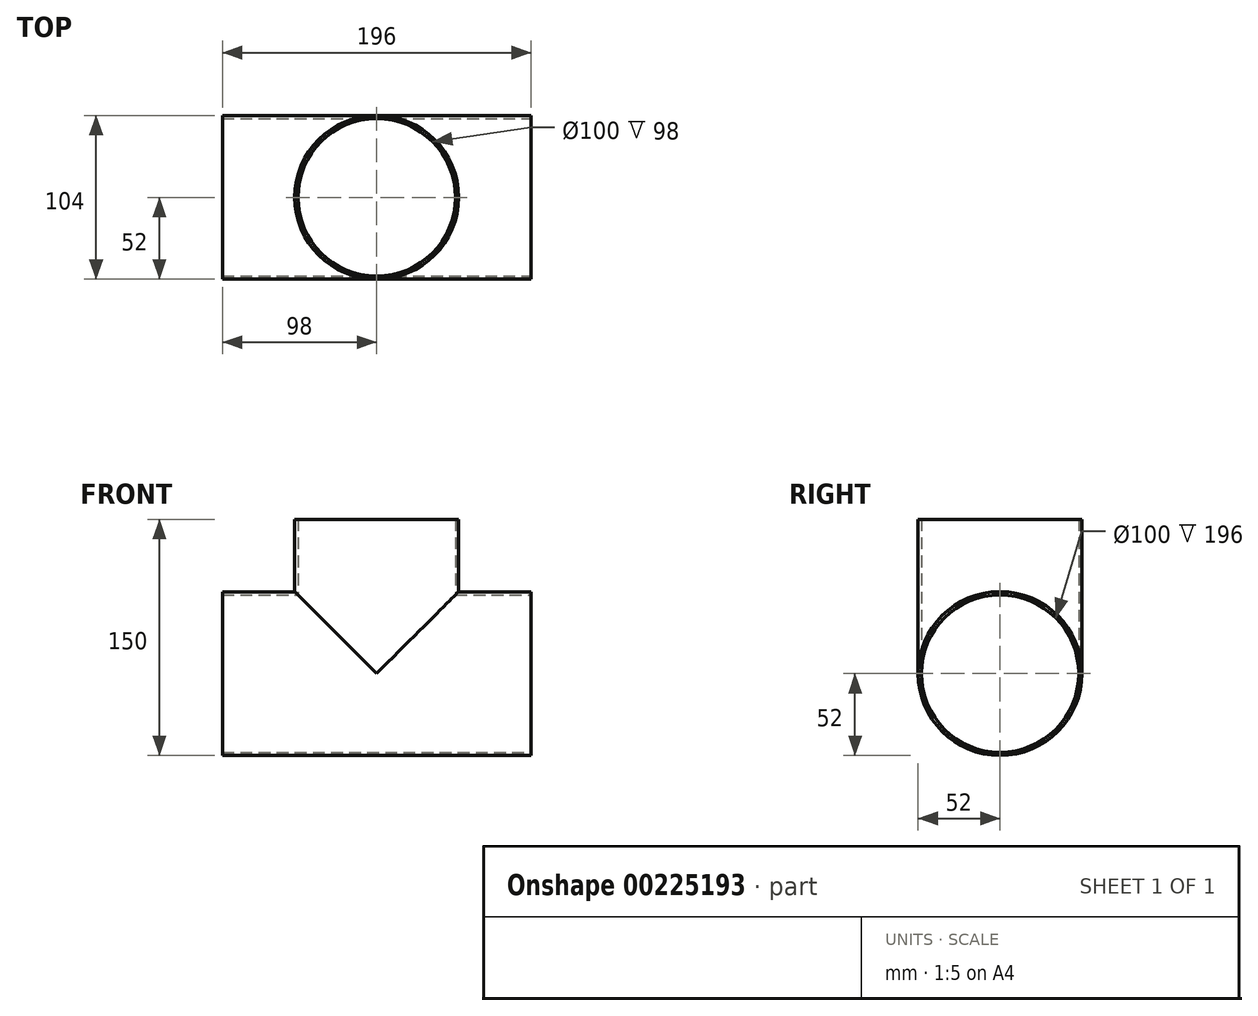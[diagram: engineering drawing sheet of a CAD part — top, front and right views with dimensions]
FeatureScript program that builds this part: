
annotation { "Feature Type Name" : "Feature", "Feature Type Description" : "" }
export const myFeature = defineFeature(function(context is Context, id is Id, definition is map)
    precondition{}
    {
        {
            var Q0;
            Q0=qCreatedBy(makeId("Right.planeOp"),FACE);
            var sketch = newSketch(context, id + "F0", { "sketchPlane" : qUnion([Q0])});
            skCircle(sketch, "E0", {"center": v(0, 0) * mm, "radius": 50 * mm});
            skCircle(sketch, "E1", {"center": v(0, 0) * mm, "radius": 52 * mm});
            skSolve(sketch);
        }
        {
            var Q0;
            Q0=qCreatedBy(makeId("Top.planeOp"),FACE);
            var sketch = newSketch(context, id + "F1", { "sketchPlane" : qUnion([Q0])});
            skCircle(sketch, "E2", {"center": v(-98, 0) * mm, "radius": 50 * mm});
            skCircle(sketch, "E3", {"center": v(-98, 0) * mm, "radius": 52 * mm});
            skSolve(sketch);
        }
        {
            var Q0;
            Q0=makeQuery(id+"F0.imprint","IMPRINT",FACE,{"disambiguationData":[TD([[makeQuery(id+"F0.imprint","IMPRINT",EDGE,{"derivedFrom":sQuery(id+"F0.wireOp",EDGE,"E0")}),-1.0]])]});
            extrude(context, id + "F2", {"entities" : qUnion([Q0]), "oppositeDirection" : true, "depth" : 196 * mm});
        }
        {
            var Q0;
            Q0=makeQuery(id+"F1.imprint","IMPRINT",FACE,{"disambiguationData":[TD([[makeQuery(id+"F1.imprint","IMPRINT",EDGE,{"derivedFrom":sQuery(id+"F1.wireOp",EDGE,"E2")}),-1.0]])]});
            extrude(context, id + "F3", {"entities" : qUnion([Q0]), "operationType" : NewBodyOperationType.ADD, "depth" : 98 * mm});
        }
        {
            var Q0;
            Q0=makeQuery(id+"F1.imprint","IMPRINT",FACE,{"disambiguationData":[TD([[makeQuery(id+"F1.imprint","IMPRINT",EDGE,{"derivedFrom":sQuery(id+"F1.wireOp",EDGE,"E2")}),1.0]])]});
            extrude(context, id + "F4", {"entities" : qUnion([Q0]), "operationType" : NewBodyOperationType.REMOVE, "depth" : 78 * mm});
        }
        {
            var Q0;
            Q0=makeQuery(id+"F0.imprint","IMPRINT",FACE,{"disambiguationData":[TD([[makeQuery(id+"F0.imprint","IMPRINT",EDGE,{"derivedFrom":sQuery(id+"F0.wireOp",EDGE,"E0")}),1.0]])]});
            extrude(context, id + "F5", {"entities" : qUnion([Q0]), "operationType" : NewBodyOperationType.REMOVE, "oppositeDirection" : true, "depth" : 188 * mm});
        }
    });
